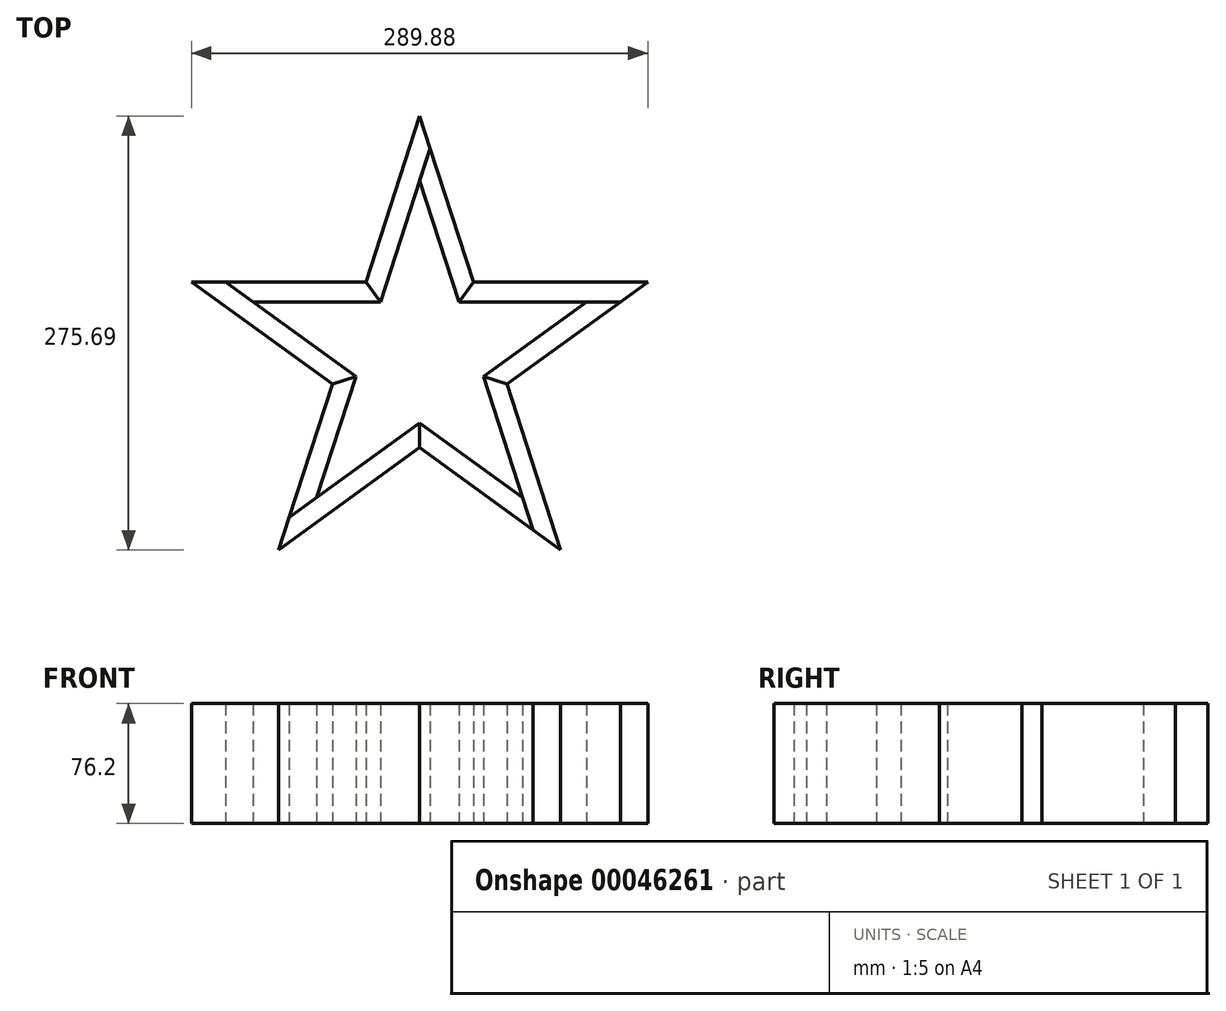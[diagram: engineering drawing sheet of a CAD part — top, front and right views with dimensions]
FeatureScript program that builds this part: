
annotation { "Feature Type Name" : "Feature", "Feature Type Description" : "" }
export const myFeature = defineFeature(function(context is Context, id is Id, definition is map)
    precondition{}
    {
        {
            var Q0;
            Q0=qCreatedBy(makeId("Top.planeOp"),FACE);
            var sketch = newSketch(context, id + "F0", { "sketchPlane" : qUnion([Q0])});
            skCircle(sketch, "E0", {"center": v(0, 0) * mm, "radius": 152.4 * mm, "construction": true});
            skCircle(sketch, "E1", {"center": v(0, 0) * mm, "radius": 58.21 * mm, "construction": true});
            skLineSegment(sketch, "E2", {"start": v(0, 152.4) * mm, "end": v(0, -58.21) * mm, "construction": true});
            skLineSegment(sketch, "E3", {"start": v(-144.94, 47.1) * mm, "end": v(55.36, -17.99) * mm, "construction": true});
            skLineSegment(sketch, "E4", {"start": v(144.94, 47.1) * mm, "end": v(-55.36, -17.99) * mm, "construction": true});
            skLineSegment(sketch, "E5", {"start": v(89.58, -123.3) * mm, "end": v(-34.22, 47.1) * mm, "construction": true});
            skLineSegment(sketch, "E6", {"start": v(-89.58, -123.3) * mm, "end": v(34.22, 47.1) * mm, "construction": true});
            skLineSegment(sketch, "E7", {"start": v(0, 152.4) * mm, "end": v(34.22, 47.1) * mm});
            skLineSegment(sketch, "E8", {"start": v(144.94, 47.1) * mm, "end": v(34.22, 47.1) * mm});
            skLineSegment(sketch, "E9", {"start": v(55.36, -17.99) * mm, "end": v(144.94, 47.1) * mm});
            skLineSegment(sketch, "E10", {"start": v(55.36, -17.99) * mm, "end": v(89.58, -123.3) * mm});
            skLineSegment(sketch, "E11", {"start": v(89.58, -123.3) * mm, "end": v(0, -58.21) * mm});
            skLineSegment(sketch, "E12", {"start": v(0, -58.21) * mm, "end": v(-89.58, -123.3) * mm});
            skLineSegment(sketch, "E13", {"start": v(-89.58, -123.3) * mm, "end": v(-55.36, -17.99) * mm});
            skLineSegment(sketch, "E14", {"start": v(-55.36, -17.99) * mm, "end": v(-144.94, 47.1) * mm});
            skLineSegment(sketch, "E15", {"start": v(-144.94, 47.1) * mm, "end": v(-34.22, 47.1) * mm});
            skLineSegment(sketch, "E16", {"start": v(-34.22, 47.1) * mm, "end": v(0, 152.4) * mm});
            skLineSegment(sketch, "E17", {"start": v(6.68, 131.85) * mm, "end": v(-24.99, 34.4) * mm});
            skLineSegment(sketch, "E18", {"start": v(0, 111.3) * mm, "end": v(24.99, 34.4) * mm});
            skLineSegment(sketch, "E19", {"start": v(34.22, 47.1) * mm, "end": v(24.99, 34.4) * mm});
            skLineSegment(sketch, "E20", {"start": v(-34.22, 47.1) * mm, "end": v(-24.99, 34.4) * mm});
            skSolve(sketch);
        }
        {
            var Q0;
            {var subQ1=sQuery(id+"F0.wireOp",EDGE,"E18");Q0=makeQuery(id+"F0.imprint","IMPRINT",FACE,{"disambiguationData":[TD([[makeQuery(id+"F0.imprint","IMPRINT",EDGE,{"derivedFrom":subQ1}),1.0]])]});}
            extrude(context, id + "F2", {"entities" : qUnion([Q0]), "depth" : 76.2 * mm});
        }
        {
            var Q0;
            {var subQ4=sQuery(id+"F0.wireOp",EDGE,"E16");Q0=makeQuery(id+"F0.imprint","IMPRINT",FACE,{"disambiguationData":[TD([[makeQuery(id+"F0.imprint","IMPRINT",EDGE,{"derivedFrom":subQ4}),-1.0]])]});}
            extrude(context, id + "F1", {"entities" : qUnion([Q0]), "depth" : 76.2 * mm});
        }
        {
            var Q0;
            Q0=qCreatedBy(makeId("Front.planeOp"),FACE);
            var sketch = newSketch(context, id + "F3", { "sketchPlane" : qUnion([Q0])});
            skLineSegment(sketch, "E21", {"start": v(0, 0) * mm, "end": v(0, 127) * mm, "construction": true});
            skSolve(sketch);
        }
        {
            var Q0;
            Q0=makeQuery(id+"F1.opExtrude","SWEPT_BODY",BODY,{"disambiguationData":[OSD([sQuery(id+"F0.wireOp",EDGE,"E7"),sQuery(id+"F0.wireOp",EDGE,"E16"),sQuery(id+"F0.wireOp",EDGE,"E17"),sQuery(id+"F0.wireOp",EDGE,"E20")])]});
            var Q1;
            Q1=makeQuery(id+"F2.opExtrude","SWEPT_BODY",BODY,{"disambiguationData":[OSD([sQuery(id+"F0.wireOp",EDGE,"E7"),sQuery(id+"F0.wireOp",EDGE,"E17"),sQuery(id+"F0.wireOp",EDGE,"E18"),sQuery(id+"F0.wireOp",EDGE,"E19")])]});
            var Q2;
            Q2=sQuery(id+"F3.wireOp",EDGE,"E21");
            circularPattern(context, id + "F4", {"entities" : qUnion([Q0, Q1]), "axis" : qUnion([Q2]), "angle" : 72 * degree, "instanceCount" : 5});
        }
    });
